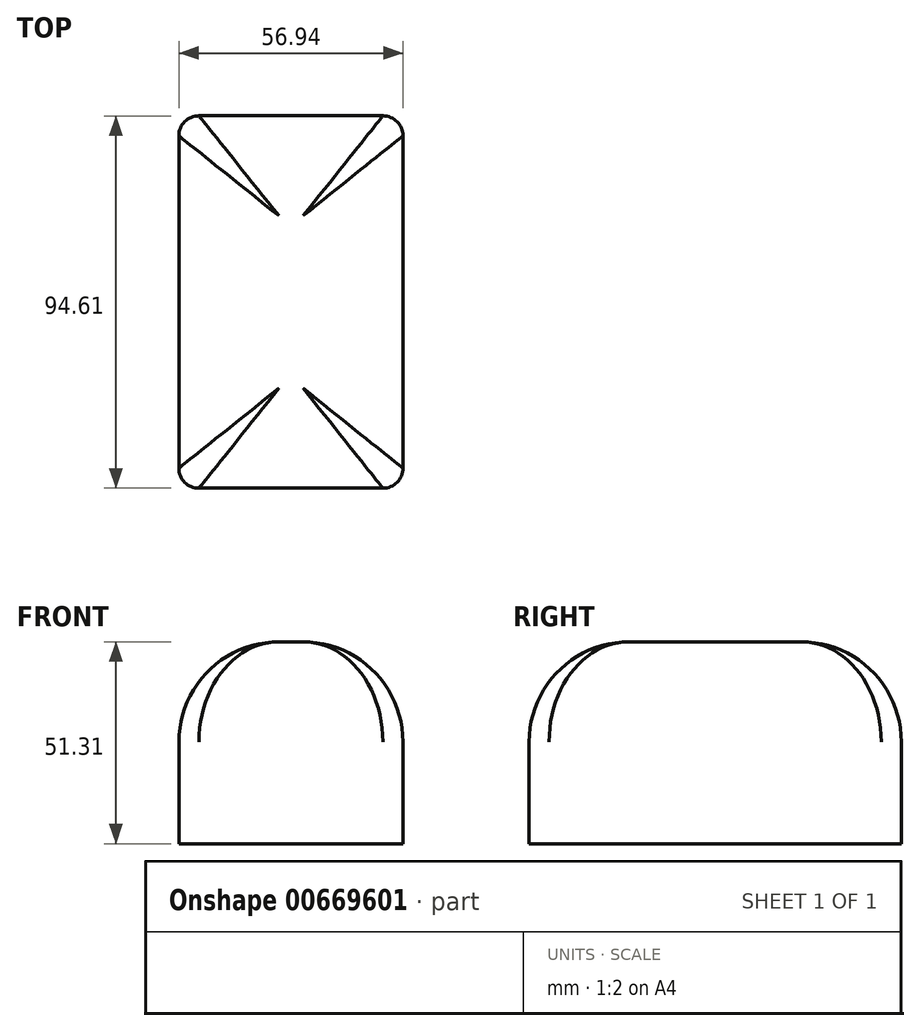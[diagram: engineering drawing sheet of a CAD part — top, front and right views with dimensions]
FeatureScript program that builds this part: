
annotation { "Feature Type Name" : "Feature", "Feature Type Description" : "" }
export const myFeature = defineFeature(function(context is Context, id is Id, definition is map)
    precondition{}
    {
        {
            var Q0;
            Q0=qCreatedBy(makeId("Top.planeOp"),FACE);
            var sketch = newSketch(context, id + "F0", { "sketchPlane" : qUnion([Q0])});
            skLineSegment(sketch, "E0.bottom", {"start": v(-97.28, -34.62) * mm, "end": v(-40.34, -34.62) * mm});
            skLineSegment(sketch, "E0.top", {"start": v(-97.28, 34.6) * mm, "end": v(-40.34, 34.6) * mm});
            skLineSegment(sketch, "E0.left", {"start": v(-97.28, -34.62) * mm, "end": v(-97.28, 34.6) * mm});
            skLineSegment(sketch, "E0.right", {"start": v(-40.34, -34.62) * mm, "end": v(-40.34, 34.6) * mm});
            skSolve(sketch);
        }
        {
            var Q0;
            Q0=makeQuery(id+"F0.imprint","IMPRINT",FACE,{"disambiguationData":[TD([[makeQuery(id+"F0.imprint","IMPRINT",EDGE,{"derivedFrom":sQuery(id+"F0.wireOp",EDGE,"E0.bottom")}),1.0]])]});
            extrude(context, id + "F1", {"entities" : qUnion([Q0]), "depth" : 51.3 * mm, "offsetDistance" : 25.4 * mm});
        }
        {
            var Q0;
            Q0=makeQuery(id+"F1.opExtrude","SWEPT_FACE",FACE,{"disambiguationData":[OSD([sQuery(id+"F0.wireOp",EDGE,"E0.bottom")])]});
            extrude(context, id + "F2", {"entities" : qUnion([Q0]), "operationType" : NewBodyOperationType.ADD, "depth" : 25.4 * mm, "offsetDistance" : 25.4 * mm});
        }
        {
            var Q0;
            {var subQ0=sQuery(id+"F0.wireOp",EDGE,"E0.bottom");Q0=makeQuery(id+"F2.boolean.opBoolean","MERGE",FACE,{"derivedFrom":[makeQuery(id+"F1.opExtrude","CAP_FACE",FACE,{"disambiguationData":[OSD([subQ0,sQuery(id+"F0.wireOp",EDGE,"E0.top"),sQuery(id+"F0.wireOp",EDGE,"E0.left"),sQuery(id+"F0.wireOp",EDGE,"E0.right")])],"isStart":false}),makeQuery(id+"F2.opExtrude","SWEPT_FACE",FACE,{"disambiguationData":[OSD([subQ0]),TDD([makeQuery(id+"F1.opExtrude","CAP_EDGE",EDGE,{"disambiguationData":[OSD([subQ0])],"isStart":false})])]})]});}
            fillet(context, id + "F3", {"entities" : qUnion([Q0]), "radius" : 25.4 * mm, "tangentPropagation" : true, "allowEdgeOverflow" : false});
        }
        {
            var Q0;
            Q0=makeQuery(id+"F3.opFillet","BLEND_FACE",FACE,{"disambiguationData":[OSD([sQuery(id+"F0.wireOp",EDGE,"E0.bottom"),sQuery(id+"F0.wireOp",EDGE,"E0.left")])]});
            var Q1;
            Q1=makeQuery(id+"F3.opFillet","BLEND_FACE",FACE,{"disambiguationData":[OSD([sQuery(id+"F0.wireOp",EDGE,"E0.top")])]});
            var Q2;
            Q2=makeQuery(id+"F3.opFillet","BLEND_FACE",FACE,{"disambiguationData":[OSD([sQuery(id+"F0.wireOp",EDGE,"E0.bottom"),sQuery(id+"F0.wireOp",EDGE,"E0.right")])]});
            var Q3;
            Q3=makeQuery(id+"F3.opFillet","BLEND_FACE",FACE,{"disambiguationData":[OSD([sQuery(id+"F0.wireOp",EDGE,"E0.bottom")])]});
            fillet(context, id + "F4", {"entities" : qUnion([Q0, Q1, Q2, Q3]), "radius" : 5.08 * mm, "tangentPropagation" : true, "allowEdgeOverflow" : false});
        }
    });
